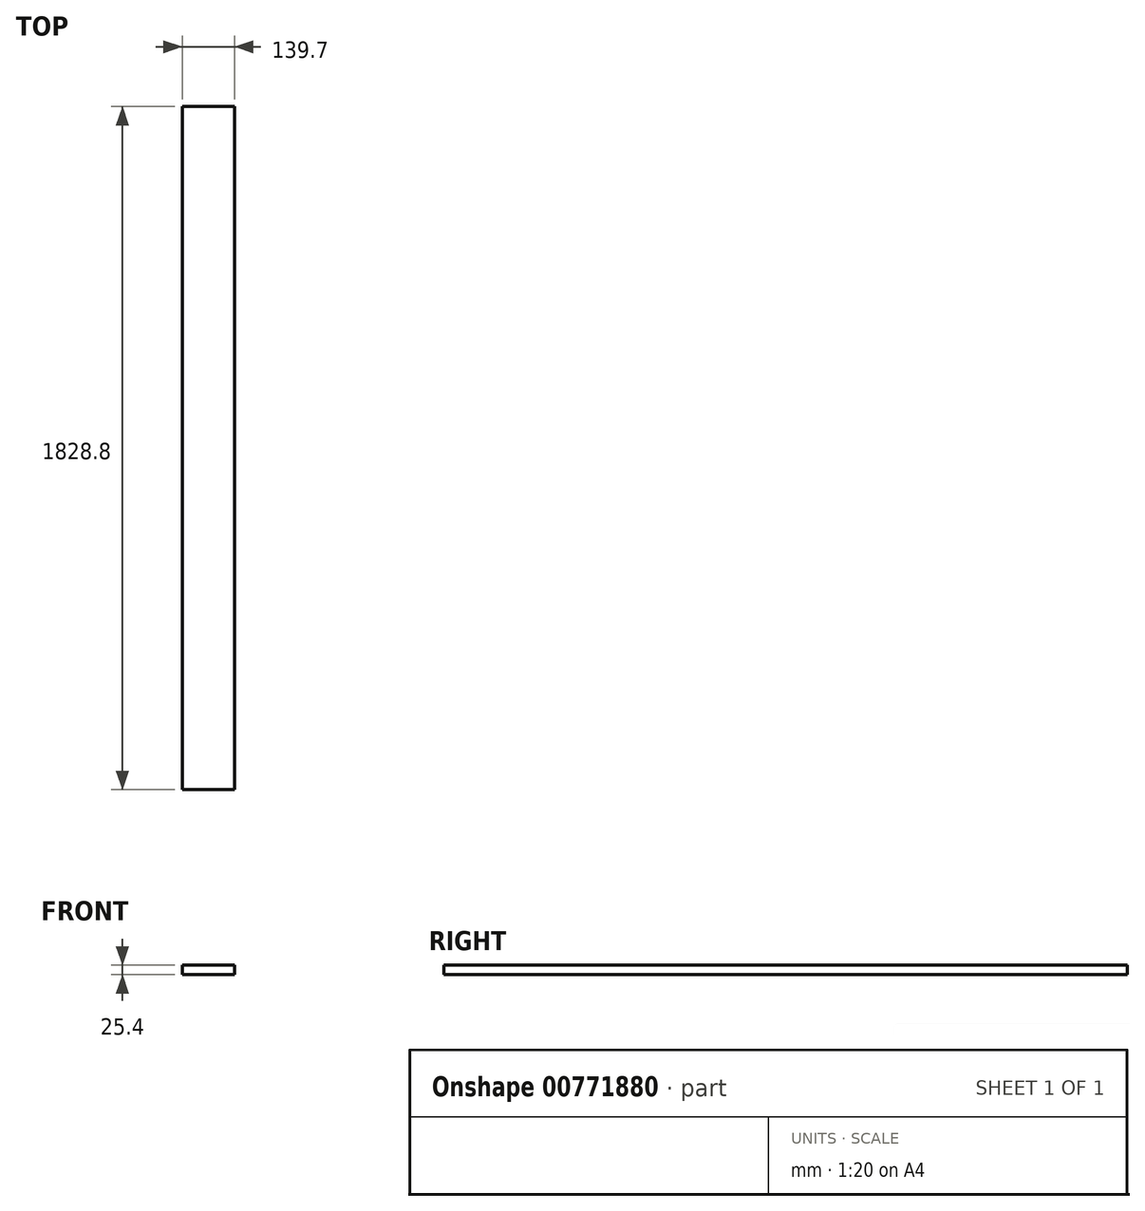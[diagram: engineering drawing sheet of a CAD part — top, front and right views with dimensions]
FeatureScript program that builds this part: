
annotation { "Feature Type Name" : "Feature", "Feature Type Description" : "" }
export const myFeature = defineFeature(function(context is Context, id is Id, definition is map)
    precondition{}
    {
        {
            var Q0;
            Q0=qCreatedBy(makeId("Front.planeOp"),FACE);
            var sketch = newSketch(context, id + "F0", { "sketchPlane" : qUnion([Q0])});
            skLineSegment(sketch, "E0.bottom", {"start": v(69.85, 12.7) * mm, "end": v(-69.85, 12.7) * mm});
            skLineSegment(sketch, "E0.top", {"start": v(69.85, -12.7) * mm, "end": v(-69.85, -12.7) * mm});
            skLineSegment(sketch, "E0.left", {"start": v(69.85, 12.7) * mm, "end": v(69.85, -12.7) * mm});
            skLineSegment(sketch, "E0.right", {"start": v(-69.85, 12.7) * mm, "end": v(-69.85, -12.7) * mm});
            skPoint(sketch, "E0.middle", {"position": v(0, 0) * mm});
            skSolve(sketch);
        }
        {
            var Q0;
            Q0=qSketchRegion(id+"F0",true);
            extrude(context, id + "F1", {"entities" : qUnion([Q0]), "depth" : 1828.8 * mm, "offsetDistance" : 25.4 * mm});
        }
    });
